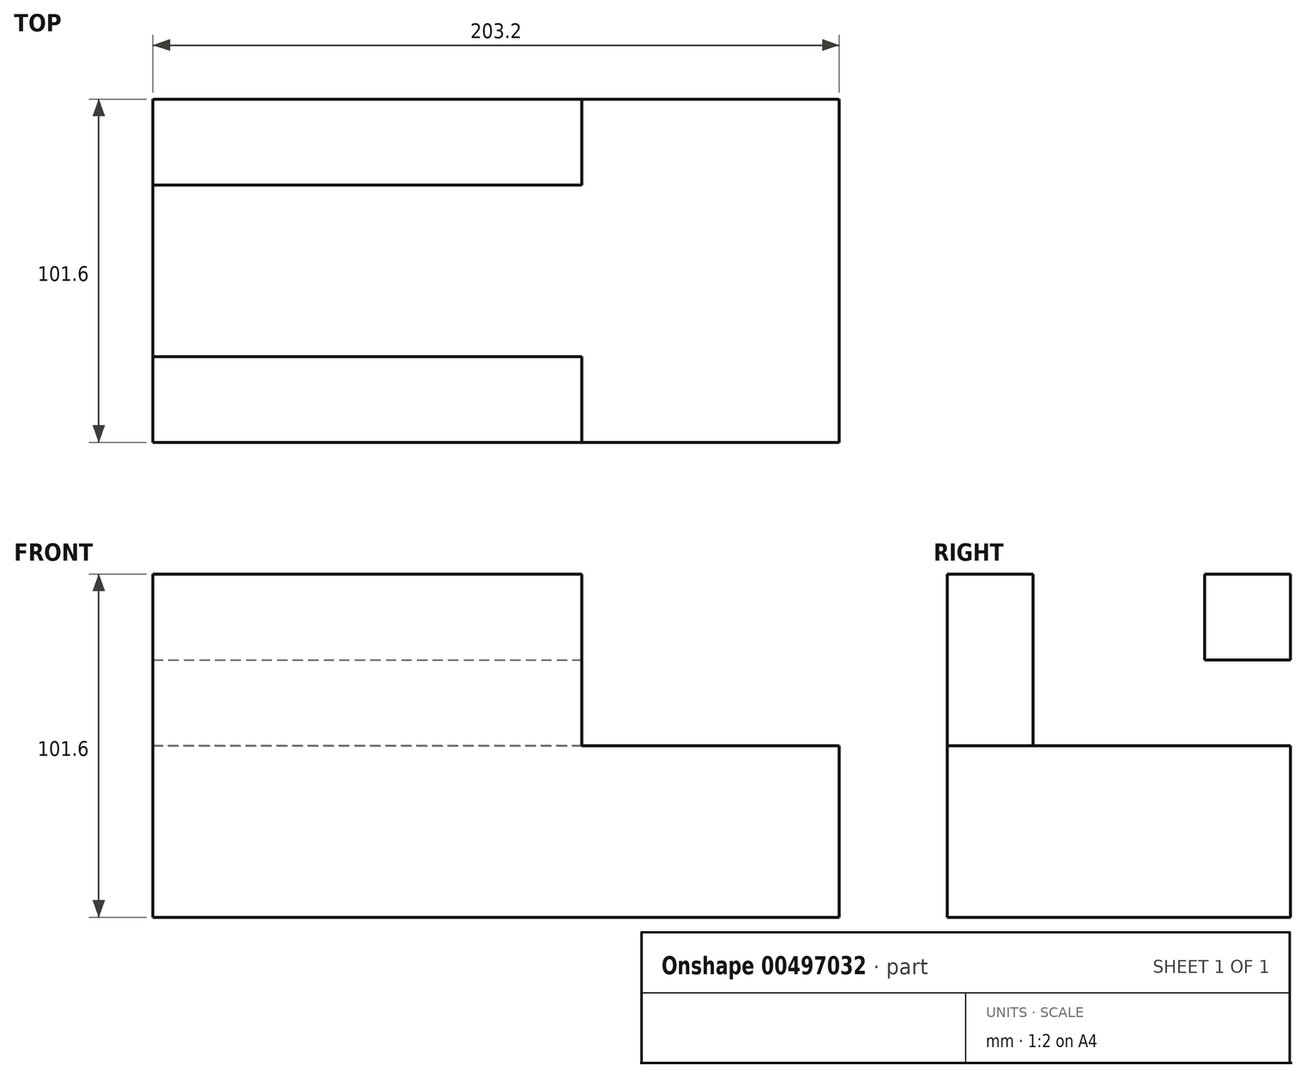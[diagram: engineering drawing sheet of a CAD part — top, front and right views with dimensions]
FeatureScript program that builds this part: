
annotation { "Feature Type Name" : "Feature", "Feature Type Description" : "" }
export const myFeature = defineFeature(function(context is Context, id is Id, definition is map)
    precondition{}
    {
        {
            var Q0;
            Q0=qCreatedBy(makeId("Front.planeOp"),FACE);
            var sketch = newSketch(context, id + "F0", { "sketchPlane" : qUnion([Q0])});
            skLineSegment(sketch, "E0.bottom", {"start": v(0, 0) * mm, "end": v(203.2, 0) * mm});
            skLineSegment(sketch, "E0.top", {"start": v(0, 50.8) * mm, "end": v(203.2, 50.8) * mm});
            skLineSegment(sketch, "E0.left", {"start": v(0, 0) * mm, "end": v(0, 50.8) * mm});
            skLineSegment(sketch, "E0.right", {"start": v(203.2, 0) * mm, "end": v(203.2, 50.8) * mm});
            skLineSegment(sketch, "E1.bottom", {"start": v(0, 50.8) * mm, "end": v(127, 50.8) * mm});
            skLineSegment(sketch, "E1.top", {"start": v(0, 76.2) * mm, "end": v(127, 76.2) * mm});
            skLineSegment(sketch, "E1.left", {"start": v(0, 50.8) * mm, "end": v(0, 76.2) * mm});
            skLineSegment(sketch, "E1.right", {"start": v(127, 50.8) * mm, "end": v(127, 76.2) * mm});
            skLineSegment(sketch, "E2.top", {"start": v(0, 101.6) * mm, "end": v(127, 101.6) * mm});
            skLineSegment(sketch, "E2.left", {"start": v(0, 76.2) * mm, "end": v(0, 101.6) * mm});
            skLineSegment(sketch, "E2.right", {"start": v(127, 76.2) * mm, "end": v(127, 101.6) * mm});
            skSolve(sketch);
        }
        {
            var Q0;
            Q0=makeQuery(id+"F0.imprint","IMPRINT",FACE,{"disambiguationData":[TD([[makeQuery(id+"F0.imprint","IMPRINT",EDGE,{"derivedFrom":sQuery(id+"F0.wireOp",EDGE,"E0.bottom")}),1.0]])]});
            var Q1;
            Q1=makeQuery(id+"F0.imprint","IMPRINT",FACE,{"disambiguationData":[TD([[makeQuery(id+"F0.imprint","IMPRINT",EDGE,{"derivedFrom":sQuery(id+"F0.wireOp",EDGE,"E1.bottom")}),1.0]])]});
            extrude(context, id + "F1", {"entities" : qUnion([Q0, Q1]), "depth" : 101.6 * mm});
        }
        {
            var Q0;
            Q0=makeQuery(id+"F0.imprint","IMPRINT",FACE,{"disambiguationData":[TD([[makeQuery(id+"F0.imprint","IMPRINT",EDGE,{"derivedFrom":sQuery(id+"F0.wireOp",EDGE,"E1.top")}),1.0]])]});
            extrude(context, id + "F2", {"entities" : qUnion([Q0]), "operationType" : NewBodyOperationType.ADD, "depth" : 25.4 * mm});
        }
        {
            var Q0;
            Q0=qCreatedBy(makeId("Top.planeOp"),FACE);
            var sketch = newSketch(context, id + "F3", { "sketchPlane" : qUnion([Q0])});
            skLineSegment(sketch, "E3.bottom", {"start": v(0, -76.2) * mm, "end": v(127, -76.2) * mm});
            skLineSegment(sketch, "E3.top", {"start": v(0, -101.6) * mm, "end": v(127, -101.6) * mm});
            skLineSegment(sketch, "E3.right", {"start": v(127, -76.2) * mm, "end": v(127, -101.6) * mm});
            skLineSegment(sketch, "E4", {"start": v(0, -101.6) * mm, "end": v(0, -76.2) * mm});
            skSolve(sketch);
        }
        {
            var Q0;
            Q0=makeQuery(id+"F3.imprint","IMPRINT",FACE,{"disambiguationData":[TD([[makeQuery(id+"F3.imprint","IMPRINT",EDGE,{"derivedFrom":sQuery(id+"F3.wireOp",EDGE,"E3.bottom")}),-1.0]])]});
            extrude(context, id + "F4", {"entities" : qUnion([Q0]), "operationType" : NewBodyOperationType.ADD, "depth" : 101.6 * mm});
        }
    });
